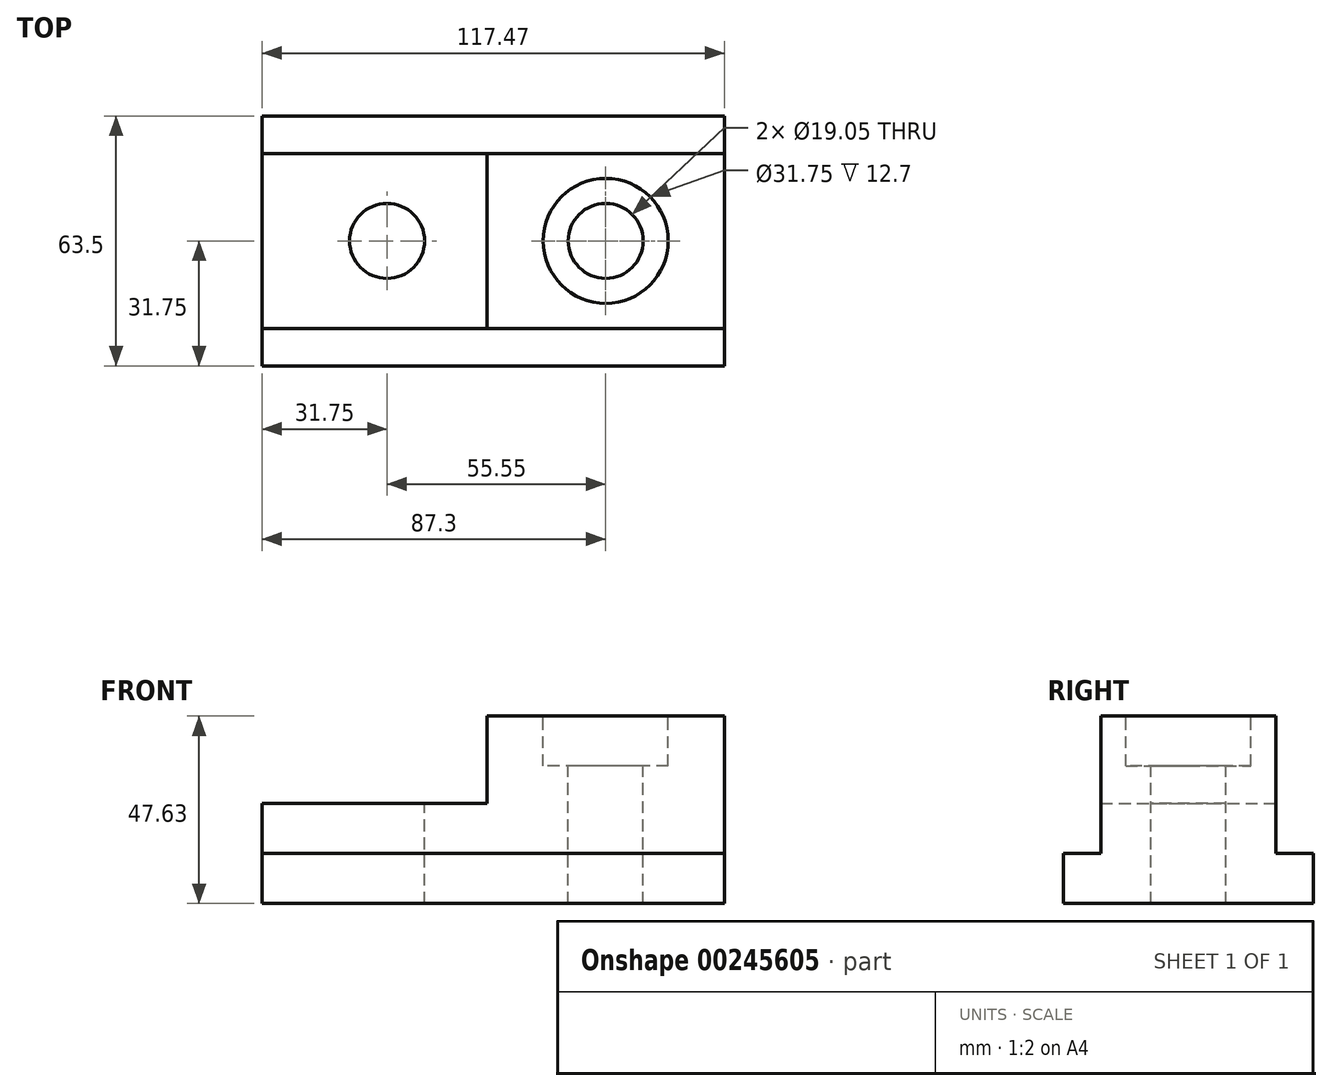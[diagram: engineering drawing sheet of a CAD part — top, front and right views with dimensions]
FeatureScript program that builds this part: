
annotation { "Feature Type Name" : "Feature", "Feature Type Description" : "" }
export const myFeature = defineFeature(function(context is Context, id is Id, definition is map)
    precondition{}
    {
        {
            var Q0;
            Q0=qCreatedBy(makeId("Top.planeOp"),FACE);
            var sketch = newSketch(context, id + "F0", { "sketchPlane" : qUnion([Q0])});
            skLineSegment(sketch, "E0.bottom", {"start": v(0, 0) * mm, "end": v(117.48, 0) * mm});
            skLineSegment(sketch, "E0.top", {"start": v(0, 63.5) * mm, "end": v(117.47, 63.5) * mm});
            skLineSegment(sketch, "E0.left", {"start": v(0, 0) * mm, "end": v(0, 63.5) * mm});
            skLineSegment(sketch, "E0.right", {"start": v(117.48, 0) * mm, "end": v(117.47, 63.5) * mm});
            skSolve(sketch);
        }
        {
            var Q0;
            Q0 = qSketchRegion(id + "F0", true);
            extrude(context, id + "F1", {"entities" : qUnion([Q0]), "depth" : 12.7 * mm});
        }
        {
            var Q0;
            Q0=makeQuery(id+"F1.opExtrude","CAP_FACE",FACE,{"disambiguationData":[OSD([sQuery(id+"F0.wireOp",EDGE,"E0.bottom"),sQuery(id+"F0.wireOp",EDGE,"E0.top"),sQuery(id+"F0.wireOp",EDGE,"E0.left"),sQuery(id+"F0.wireOp",EDGE,"E0.right")])],"isStart":false});
            var sketch = newSketch(context, id + "F2", { "sketchPlane" : qUnion([Q0])});
            skLineSegment(sketch, "E1.bottom", {"start": v(0, 53.98) * mm, "end": v(57.15, 53.98) * mm});
            skLineSegment(sketch, "E1.top", {"start": v(0, 9.53) * mm, "end": v(57.15, 9.53) * mm});
            skLineSegment(sketch, "E1.left", {"start": v(0, 53.98) * mm, "end": v(0, 9.52) * mm});
            skLineSegment(sketch, "E1.right", {"start": v(57.15, 53.98) * mm, "end": v(57.15, 9.52) * mm});
            skSolve(sketch);
        }
        {
            var Q0;
            Q0=makeQuery(id+"F2.imprint","IMPRINT",FACE,{"disambiguationData":[TD([[makeQuery(id+"F2.imprint","IMPRINT",EDGE,{"derivedFrom":sQuery(id+"F2.wireOp",EDGE,"E1.bottom")}),-1.0]])]});
            extrude(context, id + "F3", {"entities" : qUnion([Q0]), "operationType" : NewBodyOperationType.ADD, "depth" : 12.7 * mm});
        }
        {
            var Q0;
            Q0=makeQuery(id+"F1.opExtrude","CAP_FACE",FACE,{"disambiguationData":[OSD([sQuery(id+"F0.wireOp",EDGE,"E0.bottom"),sQuery(id+"F0.wireOp",EDGE,"E0.top"),sQuery(id+"F0.wireOp",EDGE,"E0.left"),sQuery(id+"F0.wireOp",EDGE,"E0.right")])],"isStart":false});
            var sketch = newSketch(context, id + "F4", { "sketchPlane" : qUnion([Q0])});
            skLineSegment(sketch, "E2.bottom", {"start": v(57.15, 9.52) * mm, "end": v(117.47, 9.52) * mm});
            skLineSegment(sketch, "E2.top", {"start": v(57.15, 53.98) * mm, "end": v(117.47, 53.98) * mm});
            skLineSegment(sketch, "E2.left", {"start": v(57.15, 9.52) * mm, "end": v(57.15, 53.98) * mm});
            skLineSegment(sketch, "E2.right", {"start": v(117.47, 9.52) * mm, "end": v(117.47, 53.98) * mm});
            skSolve(sketch);
        }
        {
            var Q0;
            Q0=makeQuery(id+"F4.imprint","IMPRINT",FACE,{"disambiguationData":[TD([[makeQuery(id+"F4.imprint","IMPRINT",EDGE,{"derivedFrom":sQuery(id+"F4.wireOp",EDGE,"E2.bottom")}),1.0]])]});
            extrude(context, id + "F5", {"entities" : qUnion([Q0]), "operationType" : NewBodyOperationType.ADD, "depth" : 34.92 * mm});
        }
        {
            var Q0;
            Q0=makeQuery(id+"F3.opExtrude","CAP_FACE",FACE,{"disambiguationData":[OSD([sQuery(id+"F2.wireOp",EDGE,"E1.bottom"),sQuery(id+"F2.wireOp",EDGE,"E1.top"),sQuery(id+"F2.wireOp",EDGE,"E1.left"),sQuery(id+"F2.wireOp",EDGE,"E1.right")])],"isStart":false});
            var sketch = newSketch(context, id + "F6", { "sketchPlane" : qUnion([Q0])});
            skCircle(sketch, "E3", {"center": v(31.75, 31.75) * mm, "radius": 9.53 * mm});
            skSolve(sketch);
        }
        {
            var Q0;
            Q0 = qSketchRegion(id + "F6", true);
            extrude(context, id + "F7", {"entities" : qUnion([Q0]), "operationType" : NewBodyOperationType.REMOVE, "oppositeDirection" : true, "depth" : 25.4 * mm});
        }
        {
            var Q0;
            Q0=makeQuery(id+"F5.opExtrude","CAP_FACE",FACE,{"disambiguationData":[OSD([sQuery(id+"F4.wireOp",EDGE,"E2.bottom"),sQuery(id+"F4.wireOp",EDGE,"E2.top"),sQuery(id+"F4.wireOp",EDGE,"E2.left"),sQuery(id+"F4.wireOp",EDGE,"E2.right")])],"isStart":false});
            var sketch = newSketch(context, id + "F8", { "sketchPlane" : qUnion([Q0])});
            skCircle(sketch, "E4", {"center": v(87.3, 31.75) * mm, "radius": 15.88 * mm});
            skSolve(sketch);
        }
        {
            var Q0;
            Q0 = qSketchRegion(id + "F8", true);
            extrude(context, id + "F9", {"entities" : qUnion([Q0]), "operationType" : NewBodyOperationType.REMOVE, "oppositeDirection" : true, "depth" : 12.7 * mm});
        }
        {
            var Q0;
            Q0=makeQuery(id+"F9.boolean.opBoolean","COPY",FACE,{"derivedFrom":makeQuery(id+"F9.opExtrude","CAP_FACE",FACE,{"disambiguationData":[OSD([sQuery(id+"F8.wireOp",EDGE,"E4")])],"isStart":false})});
            var sketch = newSketch(context, id + "F10", { "sketchPlane" : qUnion([Q0])});
            skCircle(sketch, "E5", {"center": v(87.3, 31.75) * mm, "radius": 9.53 * mm});
            skSolve(sketch);
        }
        {
            var Q0;
            Q0 = qSketchRegion(id + "F10", true);
            extrude(context, id + "F11", {"entities" : qUnion([Q0]), "operationType" : NewBodyOperationType.REMOVE, "oppositeDirection" : true, "depth" : 50.8 * mm});
        }
    });
